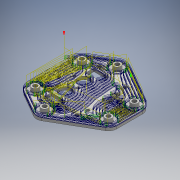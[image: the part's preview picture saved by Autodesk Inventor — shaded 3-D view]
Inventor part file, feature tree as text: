
AUTODESK INVENTOR PART (.ipt)
format: ipt  version: 2016 SP1 (Build 200210100, 210)  size: 871,424 bytes
history: native  units: mm
features: extrude x11, sketch x11, thread x6, projected_geometry x2, other x1, mirror x1, reference x1
ambient origin geometry x8: Origin, YZ Plane, XZ Plane, XY Plane, X Axis, Y Axis, Z Axis, Center Point
bodies: Solid1 (feature_tree)
feature tree (33):
  extrude  "Extrusion1"  Depth=12.0mm
  extrude  "Extrusion2"  Depth=4.0mm
  extrude  "Extrusion3"  Depth=23.0mm
  extrude  "Extrusion5"  Depth=3.0mm
  other  "Work Axis1"
  thread  "Thread1"  [1 undecoded]
  thread  "Thread2"  [1 undecoded]
  thread  "Thread3"  [1 undecoded]
  thread  "Thread4"  [1 undecoded]
  thread  "Thread5"  [1 undecoded]
  thread  "Thread6"  [1 undecoded]
  extrude  "Extrusion6"  Depth=3.0mm
  extrude  "Extrusion7"  Depth=17.0mm
  extrude  "Extrusion8"  Depth=5.0mm TaperAngle=0.0deg
  extrude  "Extrusion9"  Depth=3.0mm
  extrude  "Extrusion10"  Depth=14.0mm
  extrude  "Extrusion11"  Depth=5.0mm TaperAngle=0.0deg
  mirror  "Mirror1"
  extrude  "Extrusion12"  Depth=10.0mm
  sketch  "Sketch7"  dims[d21=3.0mm d23=21.0mm]
  sketch  "Sketch1"  dims[d0=12.0mm d1=12.0mm]
  sketch  "Sketch2"  dims[d4=4.0mm d5=4.0mm]
  sketch  "Sketch3"  dims[d6=46.0mm d7=23.0mm]
  sketch  "Sketch6"  dims[d8=28.0mm d9=28.0mm d10=12.0mm d11=12.0mm d13=30.0mm d15=360.0deg d17=5.0mm d18=0.0mm d19=3.0mm d20=3.0mm]
  reference  "Reference2"
  sketch  "Sketch8"  dims[d24=21.0mm d25=17.0mm]
  projected_geometry  "Projected Loop2"
  sketch  "Sketch9"  dims[d26=8.5mm d27=5.0mm d28=0.0mm]
  sketch  "Sketch10"  dims[d29=3.0mm d30=3.0mm]
  projected_geometry  "Projected Loop3"
  sketch  "Sketch12"  dims[d31=28.0mm d33=14.0mm]
  sketch  "Sketch13"  dims[d35=5.0mm d36=0.0mm d39=5.0mm d40=0.0mm]
  sketch  "Sketch14"  dims[d42=25.497423mm d45=9.0mm d46=9.0mm d47=9.0mm d48=22.0mm d49=22.0mm d50=10.0mm d51=0.0mm d52=10.0mm d53=0.0mm d54=10.0mm d55=0.0mm d56=10.0mm d57=0.0mm d58=10.0mm d59=0.0mm d60=10.0mm d61=0.0mm d62=1.5mm d63=1.5mm d64=1.5mm d65=1.5mm d66=1.5mm d67=1.5mm d68=2.0mm d69=0.0mm d70=2.0mm d71=0.0mm d72=2.0mm d73=2.0mm d74=0.0mm d75=0.0mm d76=0.0mm d77=25.0mm d78=25.0mm d79=2.0mm d80=0.0mm d84=8.0mm d85=15.0mm d86=2.0mm d87=2.0mm d88=0.0mm d89=3.0mm d90=8.5mm d91=30.0mm d93=360.0deg d95=10.0mm d96=0.0mm d97=8.5mm d98=0.0mm d99=30.0mm d101=360.0deg]
note: 6 required parameter values undecoded (feature->parameter linkage not recoverable at this tier; creation-order binding heuristic only, values carry confidence <= 0.55)
